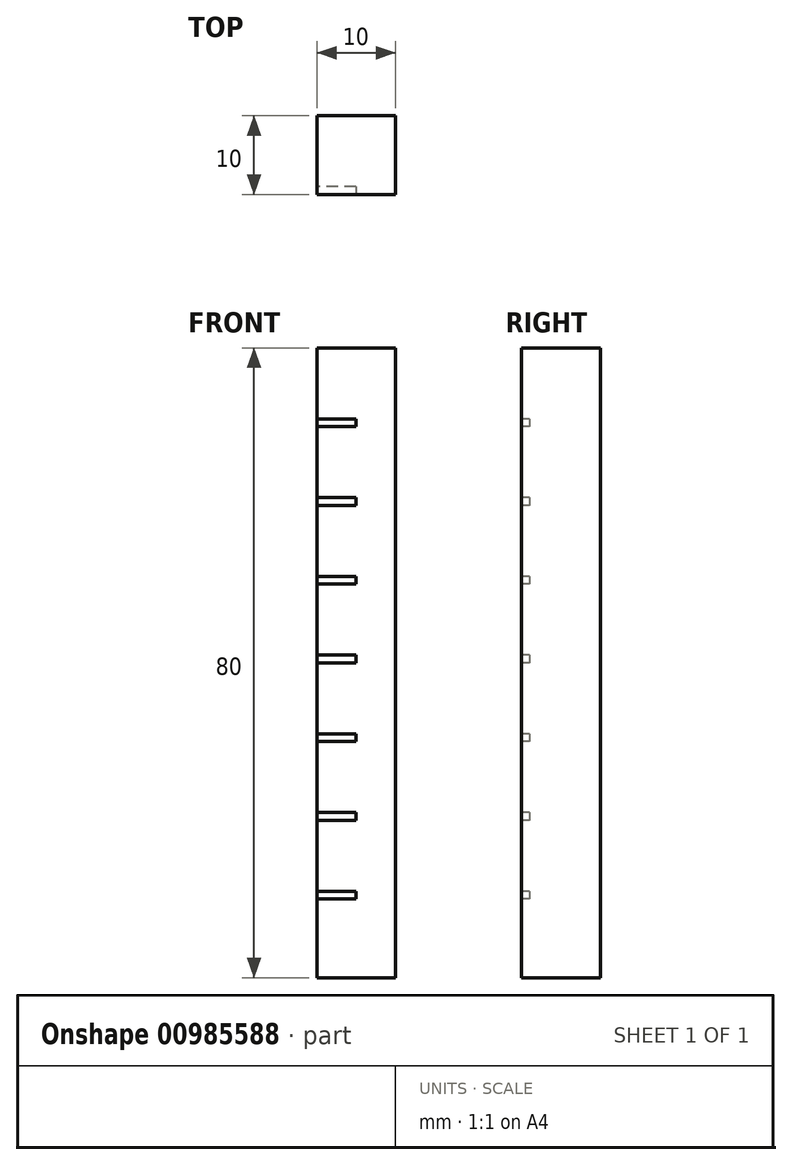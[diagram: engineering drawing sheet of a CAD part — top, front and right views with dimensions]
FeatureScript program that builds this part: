
annotation { "Feature Type Name" : "Feature", "Feature Type Description" : "" }
export const myFeature = defineFeature(function(context is Context, id is Id, definition is map)
    precondition{}
    {
        {
            var Q0;
            Q0=qCreatedBy(makeId("Top.planeOp"),FACE);
            var sketch = newSketch(context, id + "F0", { "sketchPlane" : qUnion([Q0])});
            skLineSegment(sketch, "E0.bottom", {"start": v(-5, 5) * mm, "end": v(5, 5) * mm});
            skLineSegment(sketch, "E0.top", {"start": v(-5, -5) * mm, "end": v(5, -5) * mm});
            skLineSegment(sketch, "E0.left", {"start": v(-5, 5) * mm, "end": v(-5, -5) * mm});
            skLineSegment(sketch, "E0.right", {"start": v(5, 5) * mm, "end": v(5, -5) * mm});
            skPoint(sketch, "E0.middle", {"position": v(0, 0) * mm});
            skSolve(sketch);
        }
        {
            var Q0;
            Q0=makeQuery(id+"F0.imprint","IMPRINT",FACE,{"disambiguationData":[TD([[makeQuery(id+"F0.imprint","IMPRINT",EDGE,{"derivedFrom":sQuery(id+"F0.wireOp",EDGE,"E0.bottom")}),-1.0]])]});
            extrude(context, id + "F1", {"entities" : qUnion([Q0]), "depth" : 80 * mm, "offsetDistance" : 25 * mm});
        }
        {
            var Q0;
            Q0=makeQuery(id+"F1.opExtrude","SWEPT_FACE",FACE,{"disambiguationData":[OSD([sQuery(id+"F0.wireOp",EDGE,"E0.top")])]});
            var sketch = newSketch(context, id + "F2", { "sketchPlane" : qUnion([Q0])});
            skLineSegment(sketch, "E1", {"start": v(0, 0) * mm, "end": v(0, 10) * mm});
            skLineSegment(sketch, "E2", {"start": v(0, 10) * mm, "end": v(-5, 10) * mm});
            skLineSegment(sketch, "E3", {"start": v(0, 10) * mm, "end": v(0, 20) * mm});
            skLineSegment(sketch, "E4", {"start": v(0, 20) * mm, "end": v(0, 30) * mm});
            skLineSegment(sketch, "E5", {"start": v(0, 30) * mm, "end": v(0, 40) * mm});
            skLineSegment(sketch, "E6", {"start": v(0, 40) * mm, "end": v(0, 50) * mm});
            skLineSegment(sketch, "E7", {"start": v(0, 50) * mm, "end": v(0, 60) * mm});
            skLineSegment(sketch, "E8", {"start": v(0, 60) * mm, "end": v(0, 70) * mm});
            skLineSegment(sketch, "E9", {"start": v(0, 70) * mm, "end": v(0, 80) * mm});
            skLineSegment(sketch, "E10", {"start": v(0, 10) * mm, "end": v(0, 11) * mm});
            skLineSegment(sketch, "E11", {"start": v(0, 11) * mm, "end": v(-5, 11) * mm});
            skLineSegment(sketch, "E12", {"start": v(0, 20) * mm, "end": v(-5, 20) * mm});
            skLineSegment(sketch, "E13", {"start": v(-5, 20) * mm, "end": v(-5, 21) * mm});
            skLineSegment(sketch, "E14", {"start": v(-5, 21) * mm, "end": v(0, 21) * mm});
            skLineSegment(sketch, "E15", {"start": v(0, 30) * mm, "end": v(-5, 30) * mm});
            skLineSegment(sketch, "E16", {"start": v(-5, 30) * mm, "end": v(-5, 31) * mm});
            skLineSegment(sketch, "E17", {"start": v(-5, 31) * mm, "end": v(0, 31) * mm});
            skLineSegment(sketch, "E18", {"start": v(0, 40) * mm, "end": v(-5, 40) * mm});
            skLineSegment(sketch, "E19", {"start": v(-5, 40) * mm, "end": v(-5, 41) * mm});
            skLineSegment(sketch, "E20", {"start": v(-5, 41) * mm, "end": v(0, 41) * mm});
            skLineSegment(sketch, "E21", {"start": v(0, 50) * mm, "end": v(-5, 50) * mm});
            skLineSegment(sketch, "E22", {"start": v(-5, 50) * mm, "end": v(-5, 51) * mm});
            skLineSegment(sketch, "E23", {"start": v(-5, 51) * mm, "end": v(0, 51) * mm});
            skLineSegment(sketch, "E24", {"start": v(0, 60) * mm, "end": v(-5, 60) * mm});
            skLineSegment(sketch, "E25", {"start": v(-5, 60) * mm, "end": v(-5, 61) * mm});
            skLineSegment(sketch, "E26", {"start": v(-5, 61) * mm, "end": v(0, 61) * mm});
            skLineSegment(sketch, "E27", {"start": v(0, 70) * mm, "end": v(-5, 70) * mm});
            skLineSegment(sketch, "E28", {"start": v(-5, 70) * mm, "end": v(-5, 71) * mm});
            skLineSegment(sketch, "E29", {"start": v(-5, 71) * mm, "end": v(0, 71) * mm});
            skSolve(sketch);
        }
        {
            var Q0;
            {var subQ0=sQuery(id+"F2.wireOp",EDGE,"E27");Q0=makeQuery(id+"F2.imprint","IMPRINT",FACE,{"disambiguationData":[TD([[makeQuery(id+"F2.imprint","IMPRINT",EDGE,{"derivedFrom":subQ0}),-1.0]])]});}
            var Q1;
            {var subQ0=sQuery(id+"F2.wireOp",EDGE,"E24");Q1=makeQuery(id+"F2.imprint","IMPRINT",FACE,{"disambiguationData":[TD([[makeQuery(id+"F2.imprint","IMPRINT",EDGE,{"derivedFrom":subQ0}),-1.0]])]});}
            var Q2;
            {var subQ0=sQuery(id+"F2.wireOp",EDGE,"E21");Q2=makeQuery(id+"F2.imprint","IMPRINT",FACE,{"disambiguationData":[TD([[makeQuery(id+"F2.imprint","IMPRINT",EDGE,{"derivedFrom":subQ0}),-1.0]])]});}
            var Q3;
            {var subQ0=sQuery(id+"F2.wireOp",EDGE,"E18");Q3=makeQuery(id+"F2.imprint","IMPRINT",FACE,{"disambiguationData":[TD([[makeQuery(id+"F2.imprint","IMPRINT",EDGE,{"derivedFrom":subQ0}),-1.0]])]});}
            var Q4;
            {var subQ0=sQuery(id+"F2.wireOp",EDGE,"E15");Q4=makeQuery(id+"F2.imprint","IMPRINT",FACE,{"disambiguationData":[TD([[makeQuery(id+"F2.imprint","IMPRINT",EDGE,{"derivedFrom":subQ0}),-1.0]])]});}
            var Q5;
            {var subQ0=sQuery(id+"F2.wireOp",EDGE,"E12");Q5=makeQuery(id+"F2.imprint","IMPRINT",FACE,{"disambiguationData":[TD([[makeQuery(id+"F2.imprint","IMPRINT",EDGE,{"derivedFrom":subQ0}),-1.0]])]});}
            var Q6;
            {var subQ0=sQuery(id+"F2.wireOp",EDGE,"E2");Q6=makeQuery(id+"F2.imprint","IMPRINT",FACE,{"disambiguationData":[TD([[makeQuery(id+"F2.imprint","IMPRINT",EDGE,{"derivedFrom":subQ0}),-1.0]])]});}
            extrude(context, id + "F3", {"entities" : qUnion([Q0, Q1, Q2, Q3, Q4, Q5, Q6]), "operationType" : NewBodyOperationType.REMOVE, "oppositeDirection" : true, "depth" : 1 * mm, "offsetDistance" : 25 * mm});
        }
    });
